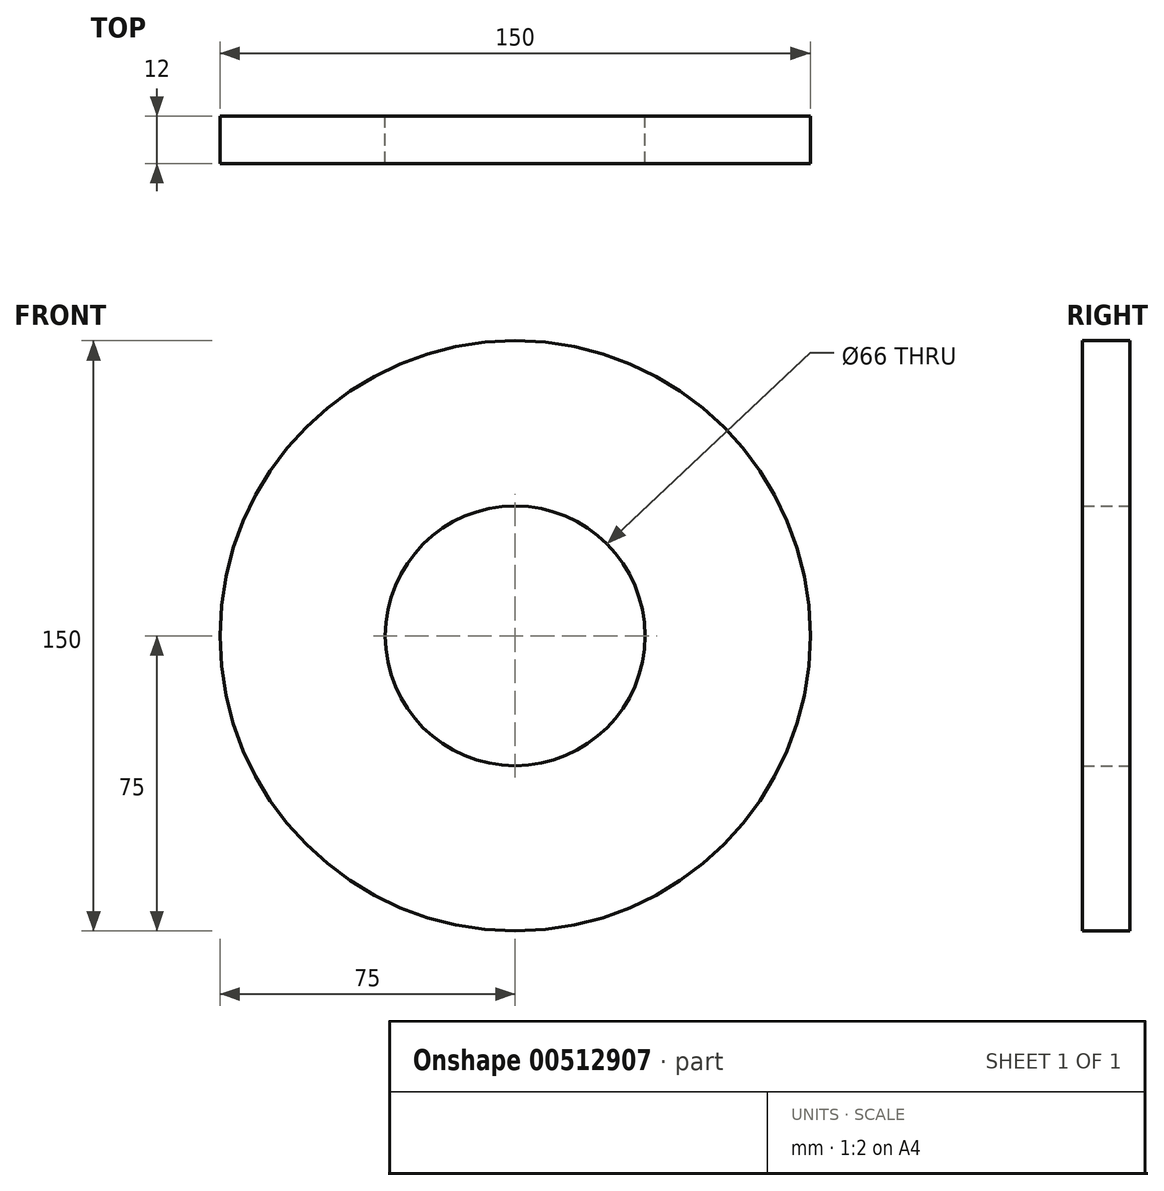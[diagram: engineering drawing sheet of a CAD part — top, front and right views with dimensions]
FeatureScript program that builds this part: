
annotation { "Feature Type Name" : "Feature", "Feature Type Description" : "" }
export const myFeature = defineFeature(function(context is Context, id is Id, definition is map)
    precondition{}
    {
        {
            var Q0;
            Q0=qCreatedBy(makeId("Front.planeOp"),FACE);
            var sketch = newSketch(context, id + "F0", { "sketchPlane" : qUnion([Q0])});
            skCircle(sketch, "E0", {"center": v(0, 0) * mm, "radius": 33 * mm});
            skCircle(sketch, "E1", {"center": v(0, 0) * mm, "radius": 75 * mm});
            skSolve(sketch);
        }
        {
            var Q0;
            Q0=makeQuery(id+"F0.imprint","IMPRINT",FACE,{"disambiguationData":[TD([[makeQuery(id+"F0.imprint","IMPRINT",EDGE,{"derivedFrom":sQuery(id+"F0.wireOp",EDGE,"E0")}),-1.0]])]});
            extrude(context, id + "F1", {"entities" : qUnion([Q0]), "depth" : 12 * mm});
        }
    });
